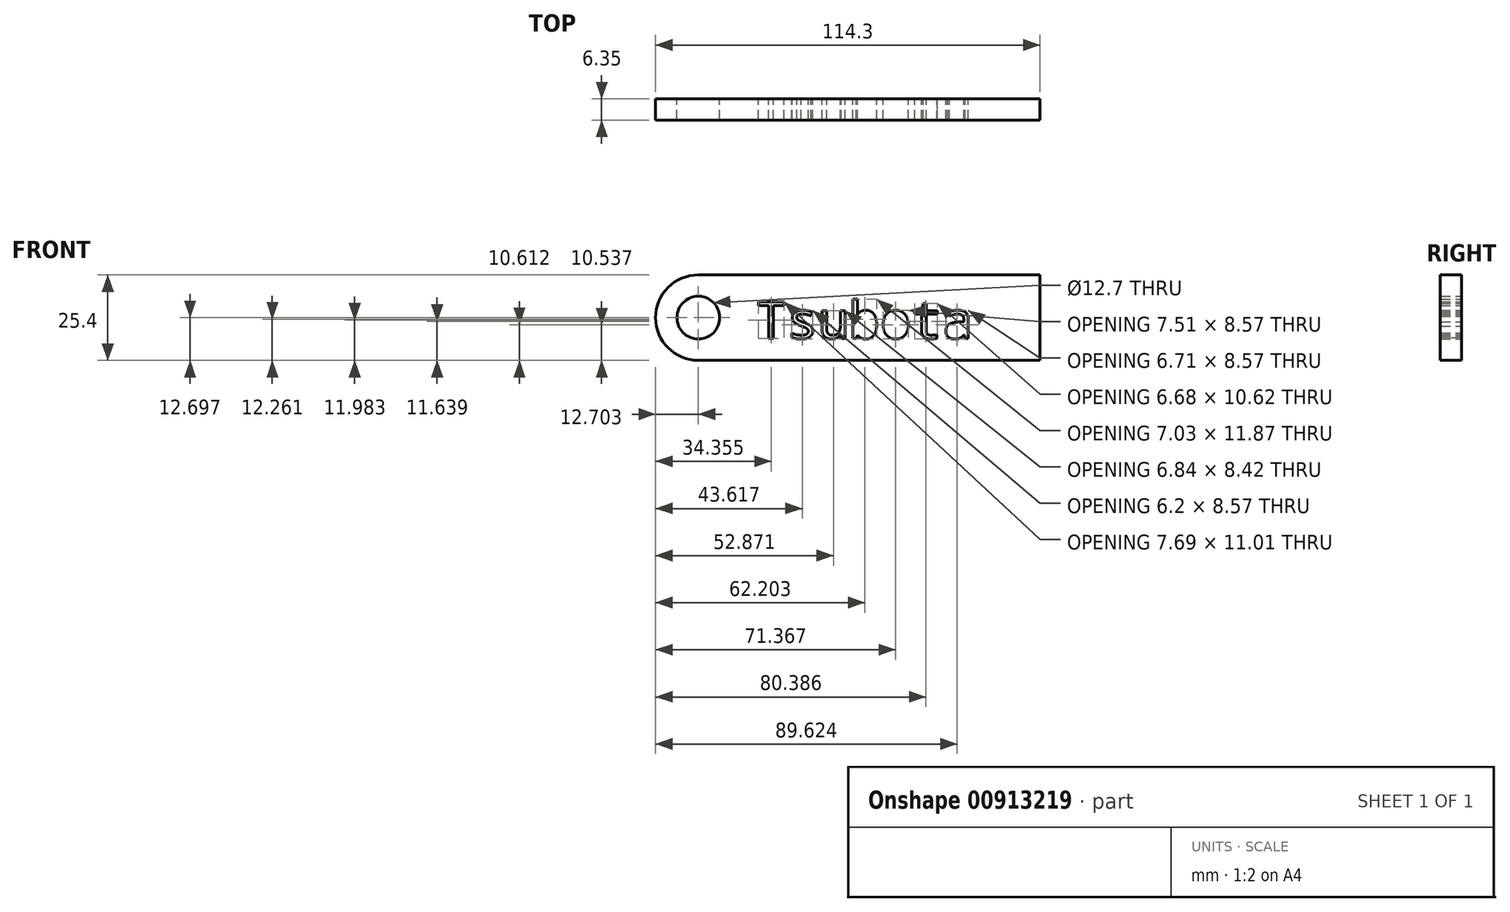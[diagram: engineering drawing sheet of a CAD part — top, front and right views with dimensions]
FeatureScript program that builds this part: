
annotation { "Feature Type Name" : "Feature", "Feature Type Description" : "" }
export const myFeature = defineFeature(function(context is Context, id is Id, definition is map)
    precondition{}
    {
        {
            var Q0;
            Q0=qCreatedBy(makeId("Front.planeOp"),FACE);
            var sketch = newSketch(context, id + "F0", { "sketchPlane" : qUnion([Q0])});
            skLineSegment(sketch, "E0", {"start": v(51.16, 15) * mm, "end": v(51.16, -10.4) * mm});
            skLineSegment(sketch, "E1", {"start": v(51.16, 15) * mm, "end": v(-50.44, 15) * mm});
            skLineSegment(sketch, "E2", {"start": v(51.16, -10.4) * mm, "end": v(-50.44, -10.4) * mm});
            skArc(sketch, "E3", {"start": v(-50.44, 15) * mm, "mid": v(-63.14, 2.3) * mm, "end": v(-50.44, -10.4) * mm});
            skCircle(sketch, "E4", {"center": v(-50.44, 2.3) * mm, "radius": 6.35 * mm});
            skText(sketch, "E5", { "text": "Tsubota", "fontName": "DroidSansMono.ttf"});
            const initialGuessF0  = {"E5": [-0.0334, -0.00392, 1, 0, 0.0111]};
            skSetInitialGuess(sketch, initialGuessF0);
            skSolve(sketch);
        }
        {
            var Q0;
            Q0 = qSketchRegion(id + "F0", true);
            extrude(context, id + "F1", {"entities" : qUnion([Q0]), "depth" : 6.35 * mm, "offsetDistance" : 25.4 * mm});
        }
    });
